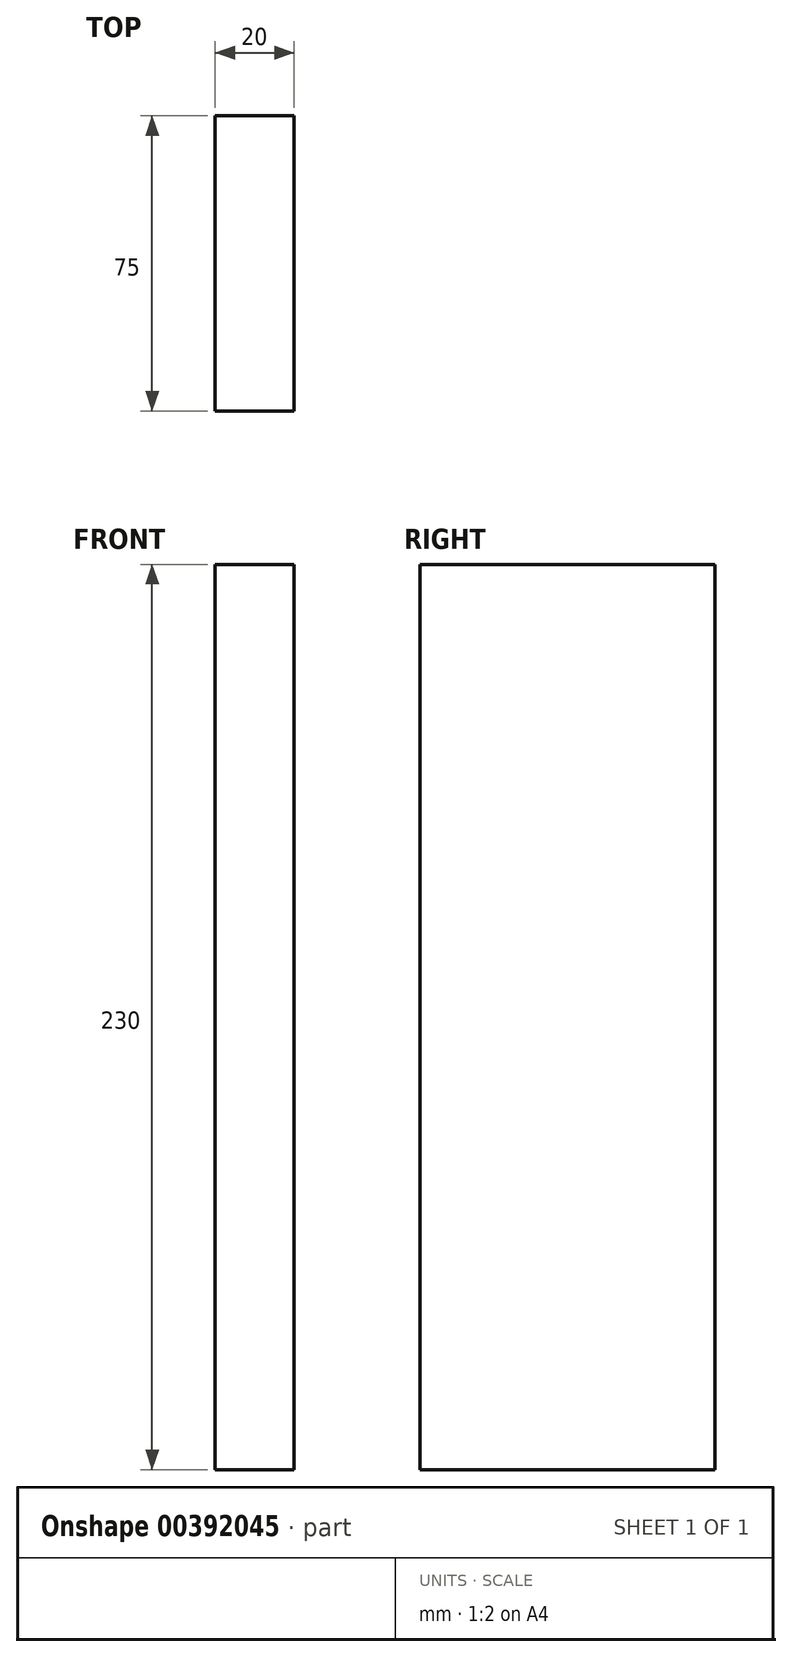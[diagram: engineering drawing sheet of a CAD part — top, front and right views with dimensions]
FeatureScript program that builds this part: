
annotation { "Feature Type Name" : "Feature", "Feature Type Description" : "" }
export const myFeature = defineFeature(function(context is Context, id is Id, definition is map)
    precondition{}
    {
        {
            var Q0;
            Q0=qCreatedBy(makeId("Top.planeOp"),FACE);
            var sketch = newSketch(context, id + "F0", { "sketchPlane" : qUnion([Q0])});
            skLineSegment(sketch, "E0.bottom", {"start": v(-10, 37.5) * mm, "end": v(10, 37.5) * mm});
            skLineSegment(sketch, "E0.top", {"start": v(-10, -37.5) * mm, "end": v(10, -37.5) * mm});
            skLineSegment(sketch, "E0.left", {"start": v(-10, 37.5) * mm, "end": v(-10, -37.5) * mm});
            skLineSegment(sketch, "E0.right", {"start": v(10, 37.5) * mm, "end": v(10, -37.5) * mm});
            skPoint(sketch, "E0.middle", {"position": v(0, 0) * mm});
            skSolve(sketch);
        }
        {
            var Q0;
            Q0 = qSketchRegion(id + "F0", true);
            extrude(context, id + "F1", {"entities" : qUnion([Q0]), "endBound" : BoundingType.SYMMETRIC, "depth" : 230 * mm});
        }
    });
